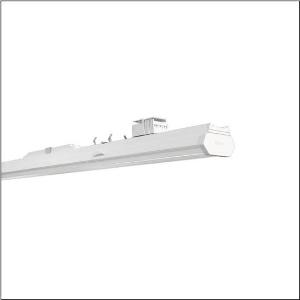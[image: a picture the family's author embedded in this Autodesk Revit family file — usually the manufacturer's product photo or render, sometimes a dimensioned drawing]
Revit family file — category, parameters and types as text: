
# Revit family: licross_11_protected_ho_51td11dn4f5s
name_source: partatom
category: Lighting Fixtures
units: mm (PartAtom-declared; Revit-internal decimal feet)

## family parameters
Cut with Voids When Loaded = No
Host = Face
Light Source = No
Part Type = Normal
Room Calculation Point = No
Round Connector Dimension = Use Diameter
Shared = No

## types (1)
- --- (1 x LED, 15510 lm, 87.3 W, 4000K)
    Apparent Load = 87 VA
    CIE Flux Codes = 84 94 98 99 100
    Color Rendering = 80
    Color Temperature = 4000K
    Default Elevation = 1800 mm
    Description = Licross 11 Protected HO, luminaire insert, of sheet steel, galvanised, coil coated, white, length: 1.500mm, width: 90mm, height: 101mm, LED rated luminous flux: 15.510lm, light colour: 840, SDCM (Standard Deviation of Colour Matching)MacAdam ≤ 2 SDCM (initial), control gear: DALI 2, with plug, 5-pole, with phase selection, mains connection: 220..240V, AC, 50/60Hz, rated input power: 87W, internal wiring halogen-free, primary light control with lens, of plastic, primary optical cover: cover, of PMMA, light emission: direct distribution, primary light characteristic: symmetric, protection rating (complete): IP54, insulation class (complete): insulation class I (protective earthing), certification: CE, ENEC, VDE, UKCA, protection symbol: D if used in an environment with non-conductive dust loads with corresponding accessories, impact resistance: IK06, permissible ambient temperature for indoor applications: -25..+30°C, corresponds to IFS (International Featured Standards) requirements for safety and quality in the food industry, reducing of maximum allowable ambient temperature of 5°C with ceiling mounting, LABS conformity tested according to VDMA 24364:2018-05, The light source and the operating device comply with the requirements of the Ecodesign Regulation (EU) 2019/2020 and are replaceable in accordance with this regulation, packaging unit: 1 piece
    Height = 92 mm
    Lamp = 1 x LED
    Lamp Light Flux = 15510 lm
    Lamp Power = 87.3 W
    Lamp count = 1
    Length = 1500 mm
    Luminous efficacy = 178 lm/W
    Manufacturer = Siteco
    ModVariant = No
    Model = 51TD11DN4F5S
    Mounting Place = Ceiling
    Mounting Type = Pendant
    Number of Poles = 1
    OnlyDefault = Yes
    Power Factor = 1
    Product Name = Licross 11 Protected HO
    Product group = luminaire insert | ceiling pendant
    ProductGroupID = 901
    Protection Class = Protection class I
    Protection Degree = IP 54
    RLX_Detail_Level = 1
    RLX_Emergency_Light_Flux = 0 lm
    RLX_Emergency_Type = 0
    RLX_Emergency_Type_DB = No
    RlxData = <blob elided: 24693 chars, md5=e4a034a6>
    Socket = socket
    Standby Power = 0 W
    System Light Flux = 15510 lm
    System Power = 87 W
    Type Comments = factory setting: luminous flux: 100 % | dim-lin: 254 | 589 mA
    Type Image = l_1256145.jpg
    URL = http://relux.com
    VarID = @adj_104197
    Voltage = 0 V
    Weight = 0.00 kg
    Width = 88 mm

## geometry (parser evidence)
native form markers: Blend x4, Sweep x11
no freeform markers — native parametric forms only
